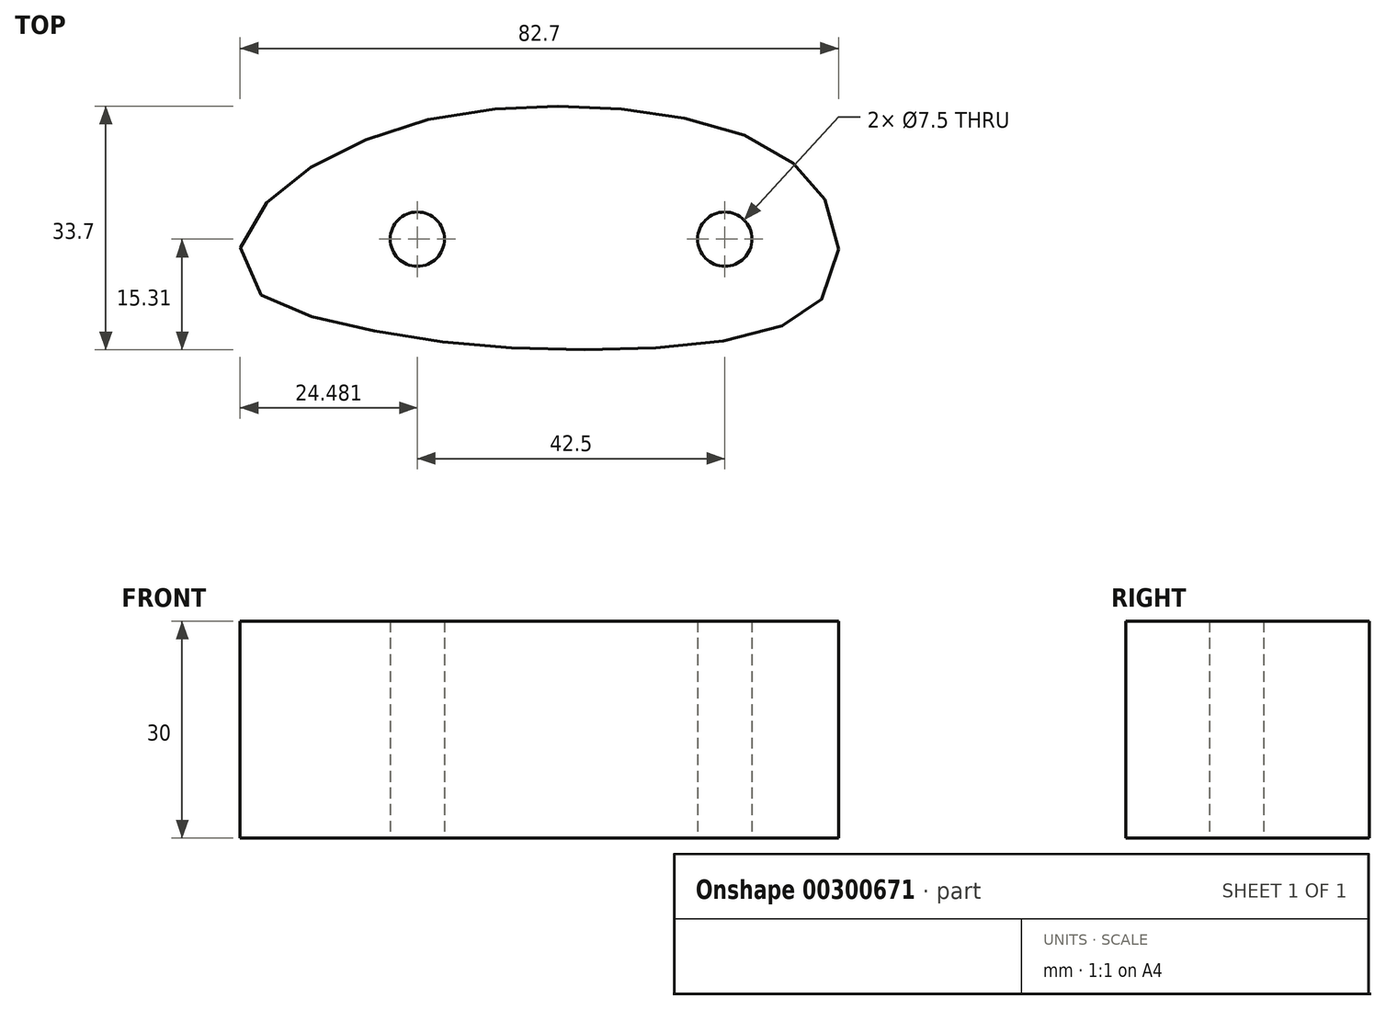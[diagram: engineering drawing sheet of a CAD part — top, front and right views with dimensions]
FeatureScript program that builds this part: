
annotation { "Feature Type Name" : "Feature", "Feature Type Description" : "" }
export const myFeature = defineFeature(function(context is Context, id is Id, definition is map)
    precondition{}
    {
        {
            var Q0;
            Q0=qCreatedBy(makeId("Top.planeOp"),FACE);
            var sketch = newSketch(context, id + "F0", { "sketchPlane" : qUnion([Q0])});
            skCircle(sketch, "E0", {"center": v(-59.35, 0) * mm, "radius": 3.75 * mm});
            skCircle(sketch, "E1", {"center": v(-16.85, 0) * mm, "radius": 3.75 * mm});
            skPoint(sketch, "E2", {"position": v(-8.61, 11.45) * mm});
            skPoint(sketch, "E3", {"position": v(-14.76, 14.6) * mm});
            skPoint(sketch, "E4", {"position": v(-22.57, 16.72) * mm});
            skPoint(sketch, "E5", {"position": v(-46.88, 18.12) * mm});
            skPoint(sketch, "E6", {"position": v(-56.18, 16.9) * mm});
            skPoint(sketch, "E7", {"position": v(-64.7, 14.43) * mm});
            skPoint(sketch, "E8", {"position": v(-72.07, 11.1) * mm});
            skPoint(sketch, "E9", {"position": v(-82.03, 2.73) * mm});
            skPoint(sketch, "E10", {"position": v(-2.3, 4.08) * mm});
            skPoint(sketch, "E11", {"position": v(-2.68, -7.27) * mm});
            skPoint(sketch, "E12", {"position": v(-1.13, -1.39) * mm});
            skPoint(sketch, "E13", {"position": v(-5.9, -10.41) * mm});
            skPoint(sketch, "E14", {"position": v(-10.71, -12.68) * mm});
            skPoint(sketch, "E15", {"position": v(-18.91, -14.32) * mm});
            skPoint(sketch, "E16", {"position": v(-28.42, -15.14) * mm});
            skPoint(sketch, "E17", {"position": v(-39.01, -15.29) * mm});
            skPoint(sketch, "E18", {"position": v(-49.73, -14.81) * mm});
            skPoint(sketch, "E19", {"position": v(-59.2, -13.75) * mm});
            skPoint(sketch, "E20", {"position": v(-68.84, -11.96) * mm});
            skPoint(sketch, "E21", {"position": v(-76.08, -10.1) * mm});
            skPoint(sketch, "E22", {"position": v(-81.33, -7.38) * mm});
            skPoint(sketch, "E23", {"position": v(-83.83, -2.2) * mm});
            skPoint(sketch, "E24", {"position": v(-38.98, 18.38) * mm});
            skPoint(sketch, "E25", {"position": v(-30.68, 17.93) * mm});
            skPoint(sketch, "E26", {"position": v(-77.77, 7.24) * mm});
            skPoint(sketch, "E27", {"position": v(-5.01, 8.11) * mm});
            skFitSpline(sketch, "E28", {"points": [v(-1.13, -1.39) * mm, v(-2.3, 4.08) * mm, v(-5.01, 8.11) * mm, v(-8.61, 11.45) * mm, v(-14.76, 14.6) * mm, v(-22.57, 16.72) * mm, v(-30.68, 17.93) * mm, v(-38.98, 18.38) * mm, v(-46.88, 18.12) * mm, v(-56.18, 16.9) * mm, v(-64.7, 14.43) * mm, v(-72.07, 11.1) * mm, v(-77.77, 7.24) * mm, v(-82.03, 2.73) * mm, v(-83.83, -2.2) * mm, v(-81.33, -7.38) * mm, v(-76.08, -10.1) * mm, v(-68.84, -11.96) * mm, v(-59.2, -13.75) * mm, v(-49.73, -14.81) * mm, v(-39.01, -15.29) * mm, v(-28.42, -15.14) * mm, v(-18.91, -14.32) * mm, v(-10.71, -12.68) * mm, v(-5.9, -10.41) * mm, v(-2.68, -7.27) * mm, v(-1.13, -1.39) * mm]});
            skLineSegment(sketch, "E29", {"start": v(-59.35, 0) * mm, "end": v(-16.85, 0) * mm});
            skSolve(sketch);
        }
        {
            var Q0;
            Q0=makeQuery(id+"F0.imprint","IMPRINT",FACE,{"disambiguationData":[TD([[makeQuery(id+"F0.imprint","IMPRINT",EDGE,{"derivedFrom":sQuery(id+"F0.wireOp",EDGE,"E0")}),-1.0]])]});
            extrude(context, id + "F1", {"entities" : qUnion([Q0]), "depth" : 30 * mm});
        }
    });
